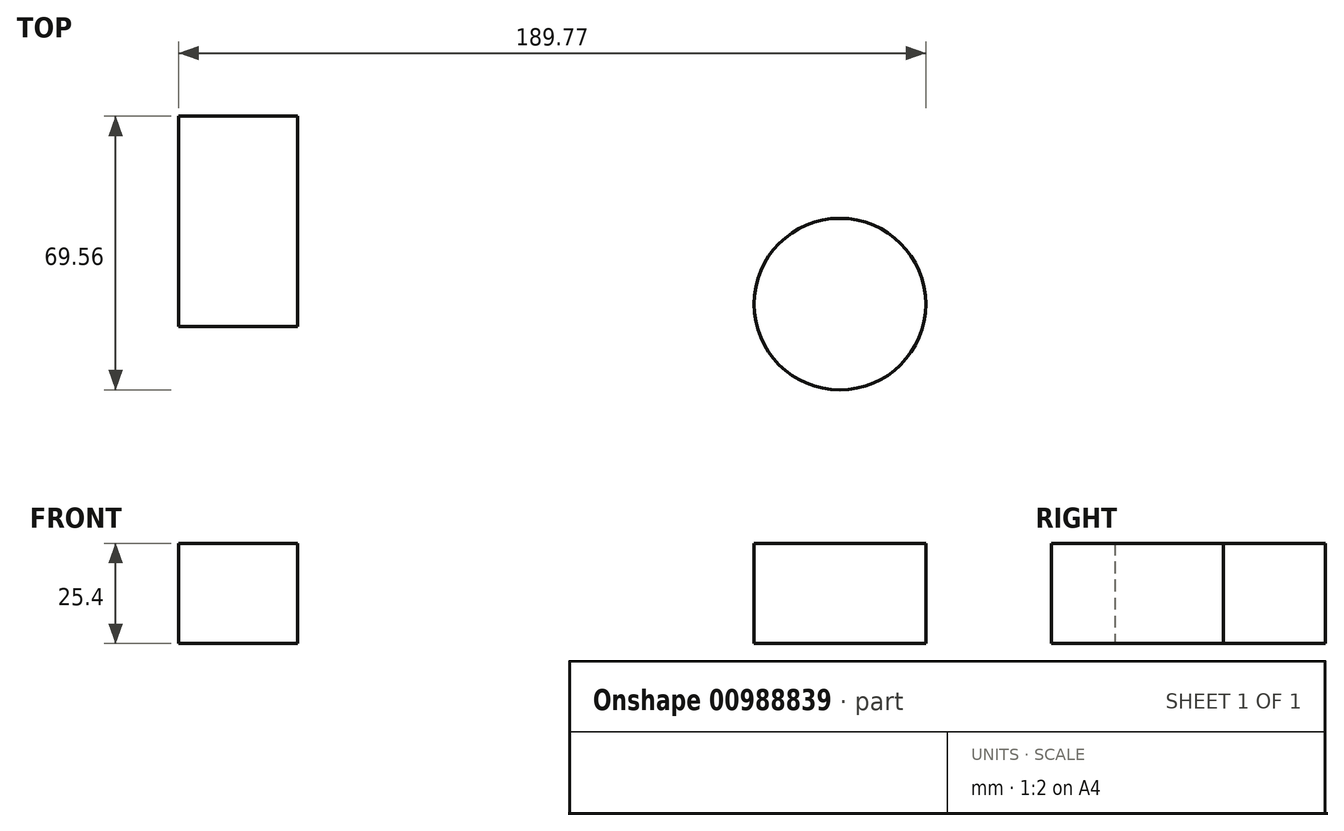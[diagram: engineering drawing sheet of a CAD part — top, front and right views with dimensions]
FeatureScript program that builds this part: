
annotation { "Feature Type Name" : "Feature", "Feature Type Description" : "" }
export const myFeature = defineFeature(function(context is Context, id is Id, definition is map)
    precondition{}
    {
        {
            var Q0;
            Q0=qCreatedBy(makeId("Top.planeOp"),FACE);
            var sketch = newSketch(context, id + "F0", { "sketchPlane" : qUnion([Q0])});
            skLineSegment(sketch, "E0", {"start": v(-59.37, -56.12) * mm, "end": v(-12.4, 28.79) * mm});
            skCircle(sketch, "E1", {"center": v(23.74, -32.44) * mm, "radius": 21.8 * mm});
            skCircle(sketch, "E2", {"center": v(22.98, 46.06) * mm, "radius": 24.5 * mm});
            skPoint(sketch, "E2.first.point", {"position": v(0, 37.59) * mm});
            skPoint(sketch, "E2.second.point", {"position": v(35.73, 25.14) * mm});
            skPoint(sketch, "E2.third.point", {"position": v(22.9, 70.56) * mm});
            skArc(sketch, "E3", {"start": v(-74.55, 51.94) * mm, "mid": v(-124.06, 58.75) * mm, "end": v(-93.1, 19.51) * mm});
            skLineSegment(sketch, "E4.bottom", {"start": v(-114.06, -38.18) * mm, "end": v(-144.23, -38.18) * mm});
            skLineSegment(sketch, "E4.top", {"start": v(-114.06, 15.32) * mm, "end": v(-144.23, 15.32) * mm});
            skLineSegment(sketch, "E4.left", {"start": v(-114.06, -38.18) * mm, "end": v(-114.06, 15.32) * mm});
            skLineSegment(sketch, "E4.right", {"start": v(-144.23, -38.18) * mm, "end": v(-144.23, 15.32) * mm});
            skSolve(sketch);
        }
        {
            var Q0;
            Q0=makeQuery(id+"F0.imprint","IMPRINT",FACE,{"disambiguationData":[TD([[makeQuery(id+"F0.imprint","IMPRINT",EDGE,{"derivedFrom":sQuery(id+"F0.wireOp",EDGE,"E4.bottom")}),-1.0]])]});
            extrude(context, id + "F1", {"entities" : qUnion([Q0]), "depth" : 25.4 * mm, "offsetDistance" : 25.4 * mm});
        }
        {
            var Q0;
            Q0=makeQuery(id+"F0.imprint","IMPRINT",FACE,{"disambiguationData":[TD([[makeQuery(id+"F0.imprint","IMPRINT",EDGE,{"derivedFrom":sQuery(id+"F0.wireOp",EDGE,"E1")}),1.0]])]});
            extrude(context, id + "F2", {"entities" : qUnion([Q0]), "depth" : 25.4 * mm, "offsetDistance" : 25.4 * mm});
        }
    });
